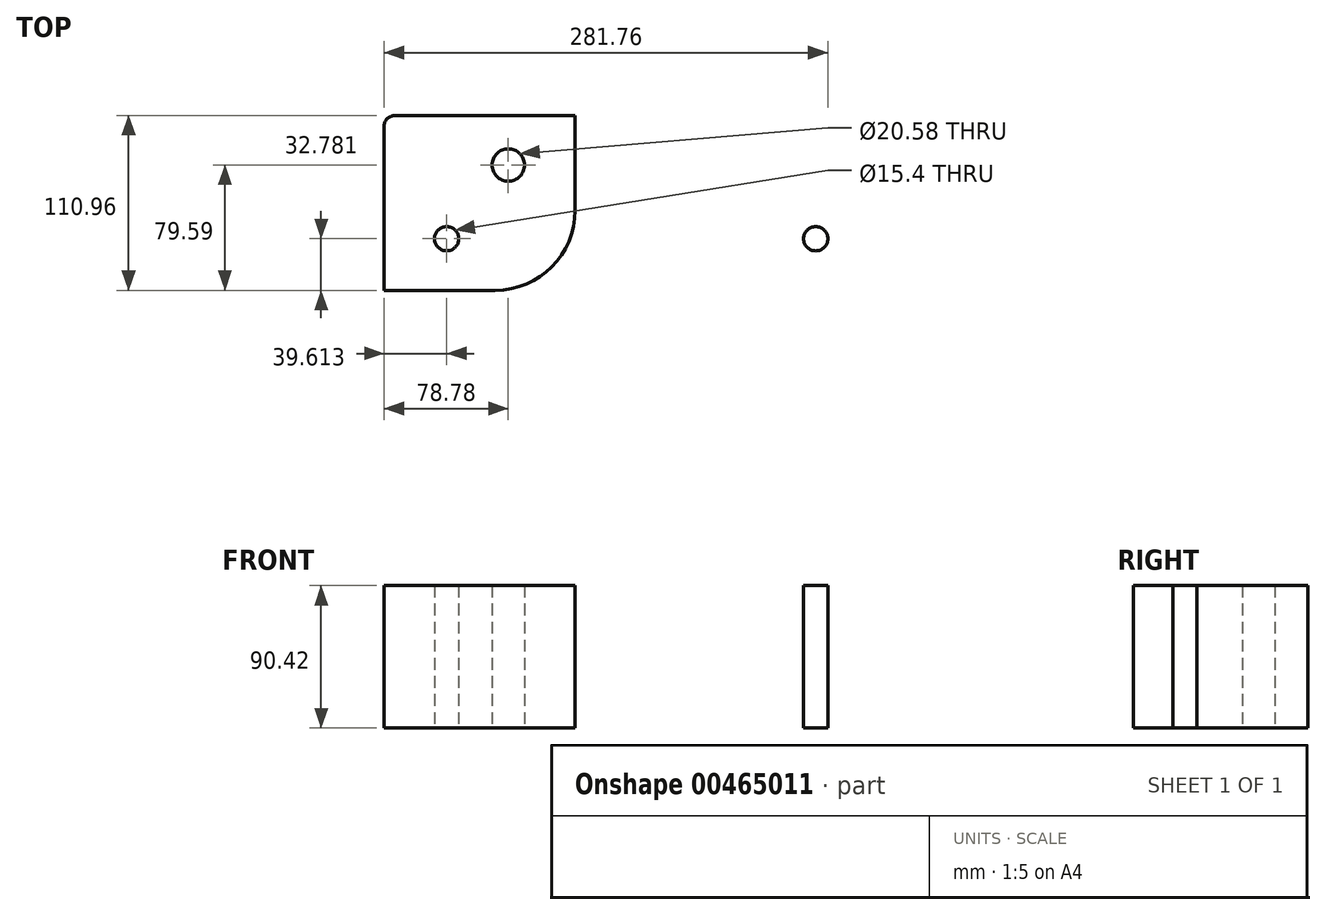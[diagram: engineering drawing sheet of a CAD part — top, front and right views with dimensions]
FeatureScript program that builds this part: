
annotation { "Feature Type Name" : "Feature", "Feature Type Description" : "" }
export const myFeature = defineFeature(function(context is Context, id is Id, definition is map)
    precondition{}
    {
        {
            var Q0;
            Q0=qCreatedBy(makeId("Top.planeOp"),FACE);
            var sketch = newSketch(context, id + "F0", { "sketchPlane" : qUnion([Q0])});
            skLineSegment(sketch, "E0.bottom", {"start": v(9.83, -55.48) * mm, "end": v(-60.63, -55.48) * mm});
            skLineSegment(sketch, "E0.top", {"start": v(60.63, 55.48) * mm, "end": v(-54.28, 55.48) * mm});
            skLineSegment(sketch, "E0.left", {"start": v(60.63, -4.68) * mm, "end": v(60.63, 55.48) * mm});
            skLineSegment(sketch, "E0.right", {"start": v(-60.63, -55.48) * mm, "end": v(-60.63, 49.13) * mm});
            skPoint(sketch, "E0.middle", {"position": v(0, 0) * mm});
            skPoint(sketch, "E1.visualSharp", {"position": v(-60.63, 55.48) * mm});
            skArc(sketch, "E1.filletArc", {"start": v(-54.28, 55.48) * mm, "mid": v(-58.77, 53.62) * mm, "end": v(-60.63, 49.13) * mm});
            skLineSegment(sketch, "E2", {"start": v(96.2, -49.2) * mm, "end": v(96.2, 64.35) * mm, "construction": true});
            skPoint(sketch, "E3.visualSharp", {"position": v(60.63, -55.48) * mm});
            skArc(sketch, "E3.filletArc", {"start": v(9.83, -55.48) * mm, "mid": v(45.75, -40.6) * mm, "end": v(60.63, -4.68) * mm});
            skCircle(sketch, "E4", {"center": v(18.15, 24.11) * mm, "radius": 10.29 * mm});
            skCircle(sketch, "E5", {"center": v(-21.02, -22.7) * mm, "radius": 7.7 * mm});
            skCircle(sketch, "E6.MirrorC", {"center": v(213.43, -22.7) * mm, "radius": 7.7 * mm});
            skLineSegment(sketch, "E7.MirrorCS", {"start": v(182.58, -55.48) * mm, "end": v(253.03, -55.48) * mm});
            skLineSegment(sketch, "E8.MirrorCS", {"start": v(131.78, -4.68) * mm, "end": v(131.78, 55.48) * mm});
            skLineSegment(sketch, "E9.MirrorCS", {"start": v(253.03, -55.48) * mm, "end": v(253.03, 49.13) * mm});
            skPoint(sketch, "E10.MirrorP", {"position": v(253.03, 55.48) * mm});
            skArc(sketch, "E11.MirrorCS", {"start": v(246.68, 55.48) * mm, "mid": v(251.17, 53.62) * mm, "end": v(253.03, 49.13) * mm});
            skPoint(sketch, "E12.MirrorP", {"position": v(131.78, -55.48) * mm});
            skLineSegment(sketch, "E13.MirrorCS", {"start": v(131.78, 55.48) * mm, "end": v(246.68, 55.48) * mm});
            skArc(sketch, "E14.MirrorCS", {"start": v(182.58, -55.48) * mm, "mid": v(146.66, -40.6) * mm, "end": v(131.78, -4.68) * mm});
            skPoint(sketch, "E15.MirrorP", {"position": v(192.4, 0) * mm});
            skCircle(sketch, "E16.MirrorC", {"center": v(174.26, 24.11) * mm, "radius": 10.29 * mm});
            skSolve(sketch);
        }
        {
            var Q0;
            Q0=makeQuery(id+"F0.imprint","IMPRINT",FACE,{"disambiguationData":[TD([[makeQuery(id+"F0.imprint","IMPRINT",EDGE,{"derivedFrom":sQuery(id+"F0.wireOp",EDGE,"E6.MirrorC")}),1.0]])]});
            var Q1;
            Q1=makeQuery(id+"F0.imprint","IMPRINT",FACE,{"disambiguationData":[TD([[makeQuery(id+"F0.imprint","IMPRINT",EDGE,{"derivedFrom":sQuery(id+"F0.wireOp",EDGE,"E0.bottom")}),-1.0]])]});
            extrude(context, id + "F1", {"entities" : qUnion([Q0, Q1]), "depth" : 90.42 * mm});
        }
    });
